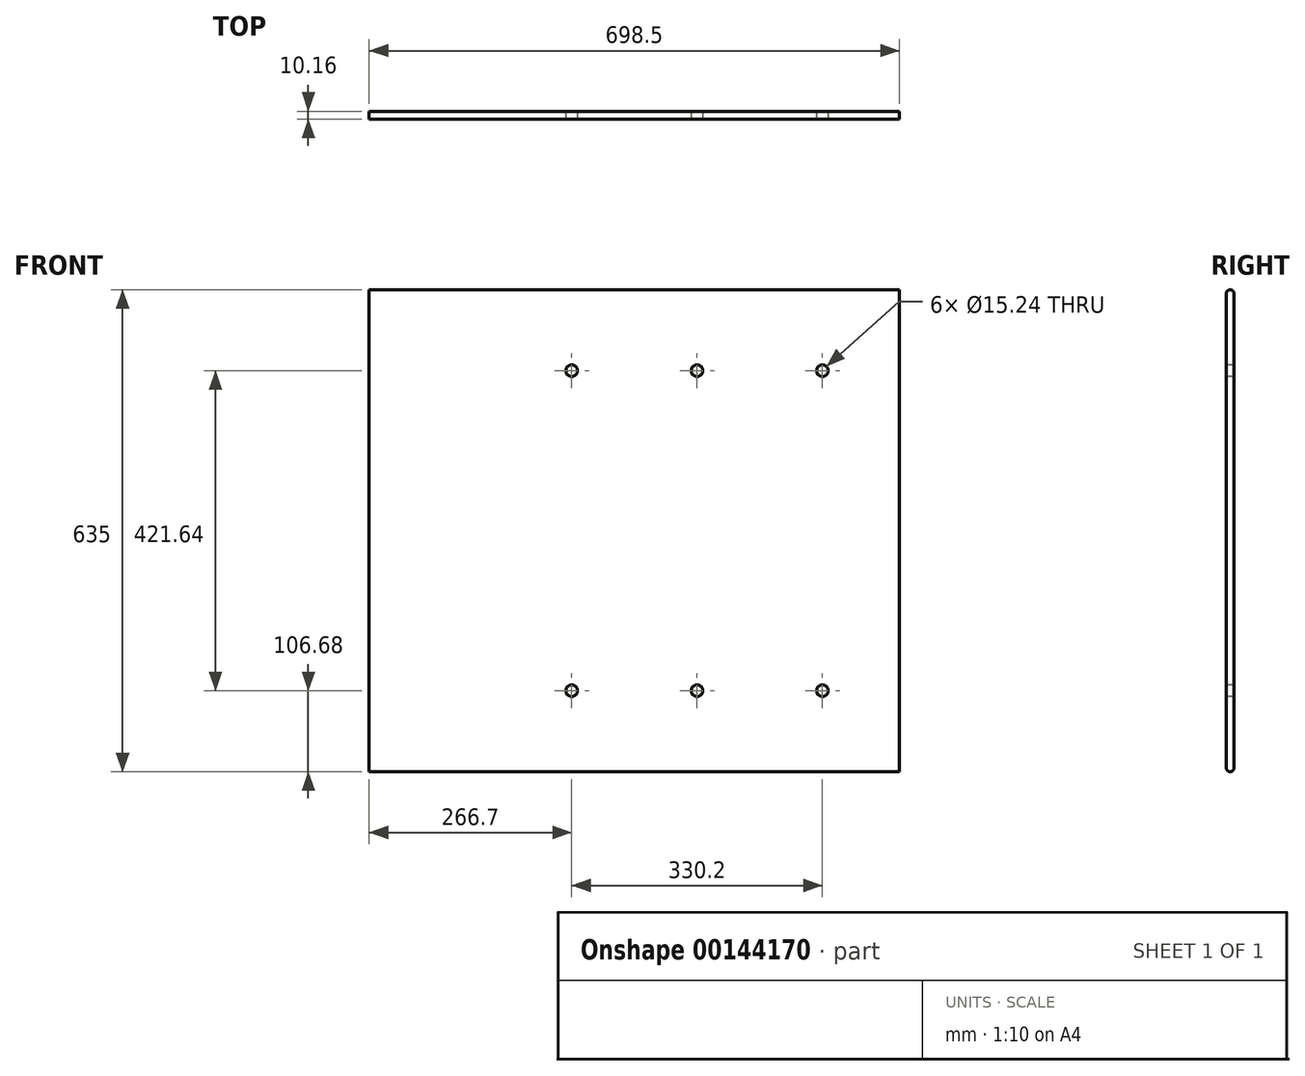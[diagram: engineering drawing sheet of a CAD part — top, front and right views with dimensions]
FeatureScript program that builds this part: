
annotation { "Feature Type Name" : "Feature", "Feature Type Description" : "" }
export const myFeature = defineFeature(function(context is Context, id is Id, definition is map)
    precondition{}
    {
        {
            var Q0;
            Q0=qCreatedBy(makeId("Front.planeOp"),FACE);
            var sketch = newSketch(context, id + "F0", { "sketchPlane" : qUnion([Q0])});
            skLineSegment(sketch, "E0.bottom", {"start": v(0, 0) * mm, "end": v(698.5, 0) * mm});
            skLineSegment(sketch, "E0.top", {"start": v(0, 635) * mm, "end": v(698.5, 635) * mm});
            skLineSegment(sketch, "E0.left", {"start": v(0, 0) * mm, "end": v(0, 635) * mm});
            skLineSegment(sketch, "E0.right", {"start": v(698.5, 0) * mm, "end": v(698.5, 635) * mm});
            skSolve(sketch);
        }
        {
            var Q0;
            Q0=makeQuery(id+"F0.imprint","IMPRINT",FACE,{"disambiguationData":[TD([[makeQuery(id+"F0.imprint","IMPRINT",EDGE,{"derivedFrom":sQuery(id+"F0.wireOp",EDGE,"E0.bottom")}),1.0]])]});
            extrude(context, id + "F1", {"entities" : qUnion([Q0]), "depth" : 10.16 * mm});
        }
        {
            var Q0;
            Q0=makeQuery(id+"F1.opExtrude","CAP_FACE",FACE,{"disambiguationData":[OSD([sQuery(id+"F0.wireOp",EDGE,"E0.bottom"),sQuery(id+"F0.wireOp",EDGE,"E0.top"),sQuery(id+"F0.wireOp",EDGE,"E0.left"),sQuery(id+"F0.wireOp",EDGE,"E0.right")])],"isStart":false});
            var sketch = newSketch(context, id + "F2", { "sketchPlane" : qUnion([Q0])});
            skLineSegment(sketch, "E1", {"start": v(0, 317.5) * mm, "end": v(50.8, 317.5) * mm, "construction": true});
            skLineSegment(sketch, "E2", {"start": v(50.8, 444.5) * mm, "end": v(50.8, 190.5) * mm, "construction": true});
            skArc(sketch, "E3.0.startCap", {"start": v(25.4, 444.5) * mm, "mid": v(50.8, 469.9) * mm, "end": v(76.2, 444.5) * mm});
            skArc(sketch, "E3.0.endCap", {"start": v(76.2, 190.5) * mm, "mid": v(50.8, 165.1) * mm, "end": v(25.4, 190.5) * mm});
            skLineSegment(sketch, "E3.0.left", {"start": v(76.2, 444.5) * mm, "end": v(76.2, 190.5) * mm});
            skLineSegment(sketch, "E3.0.right", {"start": v(25.4, 444.5) * mm, "end": v(25.4, 190.5) * mm});
            skSolve(sketch);
        }
        {
            var Q0;
            Q0=makeQuery(id+"F1.opExtrude","CAP_EDGE",EDGE,{"disambiguationData":[OSD([sQuery(id+"F0.wireOp",EDGE,"E0.top")])],"isStart":false});
            var Q1;
            Q1=makeQuery(id+"F1.opExtrude","CAP_EDGE",EDGE,{"disambiguationData":[OSD([sQuery(id+"F0.wireOp",EDGE,"E0.top")])],"isStart":true});
            var Q2;
            Q2=makeQuery(id+"F1.opExtrude","CAP_EDGE",EDGE,{"disambiguationData":[OSD([sQuery(id+"F0.wireOp",EDGE,"E0.bottom")])],"isStart":false});
            var Q3;
            Q3=makeQuery(id+"F1.opExtrude","CAP_EDGE",EDGE,{"disambiguationData":[OSD([sQuery(id+"F0.wireOp",EDGE,"E0.bottom")])],"isStart":true});
            fillet(context, id + "F3", {"entities" : qUnion([Q0, Q1, Q2, Q3]), "radius" : 5.08 * mm, "tangentPropagation" : true, "allowEdgeOverflow" : false});
        }
        {
            var Q0;
            Q0=makeQuery(id+"F2.imprint","IMPRINT",FACE,{"disambiguationData":[TD([[makeQuery(id+"F2.imprint","IMPRINT",EDGE,{"derivedFrom":sQuery(id+"F2.wireOp",EDGE,"E3.0.startCap")}),1.0]])]});
            var sketch = newSketch(context, id + "F4", { "sketchPlane" : qUnion([Q0])});
            skLineSegment(sketch, "E4.0", {"start": v(698.5, 5.08) * mm, "end": v(698.5, 629.92) * mm});
            skPoint(sketch, "E5", {"position": v(596.9, 528.32) * mm});
            skPoint(sketch, "E6.1.0.0", {"position": v(431.8, 528.32) * mm});
            skPoint(sketch, "E6.2.0.0", {"position": v(266.7, 528.32) * mm});
            skLineSegment(sketch, "E6.direction1", {"start": v(596.9, 528.32) * mm, "end": v(431.8, 528.32) * mm, "construction": true});
            skPoint(sketch, "E7", {"position": v(596.9, 106.68) * mm});
            skPoint(sketch, "E8.1.0.0", {"position": v(431.8, 106.68) * mm});
            skPoint(sketch, "E8.2.0.0", {"position": v(266.7, 106.68) * mm});
            skLineSegment(sketch, "E8.direction1", {"start": v(596.9, 106.68) * mm, "end": v(431.8, 106.68) * mm, "construction": true});
            skSolve(sketch);
        }
        {
            var Q0;
            Q0=sQuery(id+"F4.wireOp",VERTEX,"E6.1.0.0");
            var Q1;
            Q1=sQuery(id+"F4.wireOp",VERTEX,"E6.2.0.0");
            var Q2;
            Q2=sQuery(id+"F4.wireOp",VERTEX,"E5");
            var Q3;
            Q3=sQuery(id+"F4.wireOp",VERTEX,"E7");
            var Q4;
            Q4=sQuery(id+"F4.wireOp",VERTEX,"E8.1.0.0");
            var Q5;
            Q5=sQuery(id+"F4.wireOp",VERTEX,"E8.2.0.0");
            var Q6;
            Q6=makeQuery(id+"F1.opExtrude","SWEPT_BODY",BODY,{"disambiguationData":[OSD([sQuery(id+"F0.wireOp",EDGE,"E0.bottom"),sQuery(id+"F0.wireOp",EDGE,"E0.top"),sQuery(id+"F0.wireOp",EDGE,"E0.left"),sQuery(id+"F0.wireOp",EDGE,"E0.right")])]});
            hole(context, id + "F5", {"style" : HoleStyle.SIMPLE, "endStyle" : HoleEndStyle.THROUGH, "holeDiameter" : 15.24 * mm, "locations" : qUnion([Q0, Q1, Q2, Q3, Q4, Q5]), "scope" : qUnion([Q6]), "isTappedThrough" : true});
        }
    });
